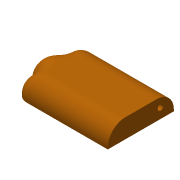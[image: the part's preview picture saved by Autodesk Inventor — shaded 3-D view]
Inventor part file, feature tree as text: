
AUTODESK INVENTOR PART (.ipt)
format: ipt  version: 2016 (Build 200138000, 138)  size: 185,344 bytes
history: native  units: mm
features: extrude x4, sketch x4, reference x3, fillet x1, plane x1
ambient origin geometry x8: Origin, YZ Plane, XZ Plane, XY Plane, X Axis, Y Axis, Z Axis, Center Point
bodies: Solid1 (feature_tree)
feature tree (13):
  extrude  "Extrusion1"  Depth=7.0mm TaperAngle=0.0deg
  extrude  "Extrusion3"  [1 undecoded]
  fillet  "Fillet2"  Radius=2.0mm
  plane  "Work Plane1"
  extrude  "Extrusion4"  Depth=45.0mm TaperAngle=0.0deg
  extrude  "Extrusion5"  [1 undecoded]
  sketch  "Sketch1"  dims[d0=11.0mm d1=0.0mm d5=7.0mm d6=0.0mm]
  reference  "Reference1"
  reference  "Reference2"
  sketch  "Sketch3"  dims[d7=10.0mm d8=-3.0mm d9=2.0mm]
  sketch  "Sketch5"  dims[d10=45.0mm d11=0.0mm d12=45.0mm d13=0.0mm]
  sketch  "Sketch6"
  reference  "Reference3"
note: 2 required parameter values undecoded (feature->parameter linkage not recoverable at this tier; creation-order binding heuristic only, values carry confidence <= 0.55)
